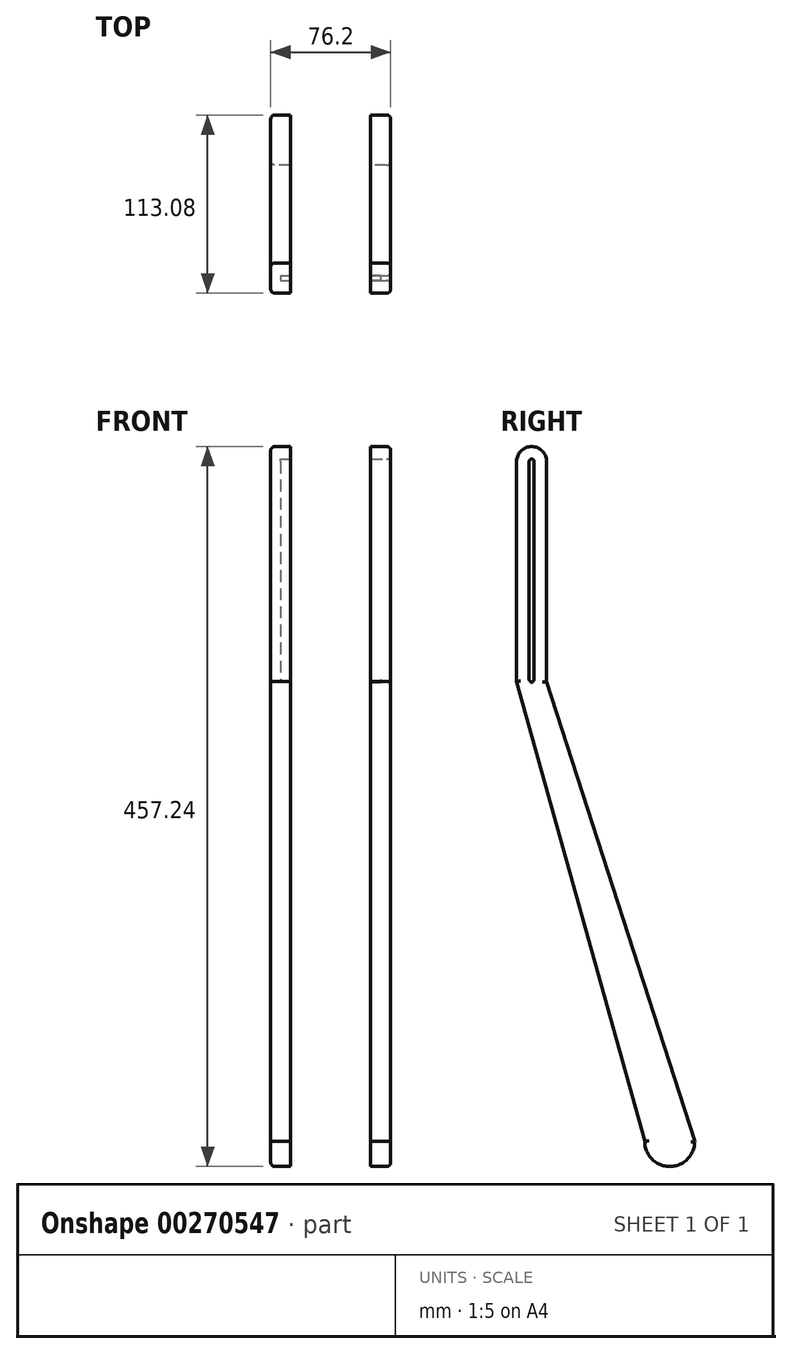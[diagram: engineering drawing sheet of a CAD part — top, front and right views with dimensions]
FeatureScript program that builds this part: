
annotation { "Feature Type Name" : "Feature", "Feature Type Description" : "" }
export const myFeature = defineFeature(function(context is Context, id is Id, definition is map)
    precondition{}
    {
        {
            var Q0;
            Q0=qCreatedBy(makeId("Right.planeOp"),FACE);
            var sketch = newSketch(context, id + "F0", { "sketchPlane" : qUnion([Q0])});
            skLineSegment(sketch, "E0", {"start": v(0, 0) * mm, "end": v(0, 355.6) * mm, "construction": true});
            skLineSegment(sketch, "E1", {"start": v(19.3, 0) * mm, "end": v(-74.73, 292.1) * mm});
            skLineSegment(sketch, "E2", {"start": v(-74.73, 292.1) * mm, "end": v(-93.78, 292.1) * mm});
            skLineSegment(sketch, "E3", {"start": v(-93.78, 292.1) * mm, "end": v(-12.45, 0) * mm});
            skLineSegment(sketch, "E4", {"start": v(-93.78, 292.1) * mm, "end": v(-93.78, 431.8) * mm});
            skLineSegment(sketch, "E5", {"start": v(-93.78, 431.8) * mm, "end": v(-74.73, 431.8) * mm});
            skLineSegment(sketch, "E6", {"start": v(-74.73, 431.8) * mm, "end": v(-74.73, 292.1) * mm});
            skArc(sketch, "E7", {"start": v(-74.73, 431.8) * mm, "mid": v(-84.26, 441.33) * mm, "end": v(-93.78, 431.8) * mm});
            skLineSegment(sketch, "E8", {"start": v(-12.45, 0) * mm, "end": v(19.3, 0) * mm});
            skArc(sketch, "E9", {"start": v(-12.45, 0) * mm, "mid": v(3.43, -15.91) * mm, "end": v(19.3, 0) * mm});
            skSolve(sketch);
        }
        {
            var Q0;
            Q0 = qSketchRegion(id + "F0", true);
            extrude(context, id + "F1", {"entities" : qUnion([Q0]), "depth" : 127 * mm});
        }
        {
            var Q0;
            Q0=makeQuery(id+"F1.opExtrude","CAP_FACE",FACE,{"disambiguationData":[OSD([sQuery(id+"F0.wireOp",EDGE,"E1"),sQuery(id+"F0.wireOp",EDGE,"E3"),sQuery(id+"F0.wireOp",EDGE,"E4"),sQuery(id+"F0.wireOp",EDGE,"E6"),sQuery(id+"F0.wireOp",EDGE,"E7"),sQuery(id+"F0.wireOp",EDGE,"vNp1OqKy-Z6YU-8cuM-Ckrt-ocsQJN6kqNDd"),sQuery(id+"F0.wireOp",EDGE,"EuecpMSg-LQ6o-H8uq-qzqB-xBjWzeGu6t28"),sQuery(id+"F0.wireOp",EDGE,"25FLd6Fp-RHUA-4MTj-8GUR-LZmMyovwXqkN"),sQuery(id+"F0.wireOp",EDGE,"Zij4NibO-UUHo-Tc3n-FIWC-QqlzmEsbWXEq")])],"isStart":false});
            var sketch = newSketch(context, id + "F2", { "sketchPlane" : qUnion([Q0])});
            skLineSegment(sketch, "E10", {"start": v(36.72, -144.12) * mm, "end": v(-159.05, 242.08) * mm});
            skLineSegment(sketch, "E11", {"start": v(-159.05, 242.08) * mm, "end": v(-331.56, 331.76) * mm});
            skLineSegment(sketch, "E12", {"start": v(-331.56, 331.76) * mm, "end": v(-175.34, 764.32) * mm});
            skLineSegment(sketch, "E13", {"start": v(-175.34, 764.32) * mm, "end": v(-62.3, 748.79) * mm});
            skLineSegment(sketch, "E14", {"start": v(-62.3, 748.79) * mm, "end": v(32.9, 331.76) * mm});
            skLineSegment(sketch, "E15", {"start": v(32.9, 331.76) * mm, "end": v(36.72, -144.12) * mm});
            skSolve(sketch);
        }
        {
            var Q0;
            Q0 = qSketchRegion(id + "F2", true);
            extrude(context, id + "F3", {"entities" : qUnion([Q0]), "operationType" : NewBodyOperationType.REMOVE, "oppositeDirection" : true, "depth" : 25.4 * mm});
        }
        {
            var Q0;
            Q0=makeQuery(id+"F1.opExtrude","CAP_FACE",FACE,{"disambiguationData":[OSD([sQuery(id+"F0.wireOp",EDGE,"E1"),sQuery(id+"F0.wireOp",EDGE,"E3"),sQuery(id+"F0.wireOp",EDGE,"E4"),sQuery(id+"F0.wireOp",EDGE,"E6"),sQuery(id+"F0.wireOp",EDGE,"E7"),sQuery(id+"F0.wireOp",EDGE,"vNp1OqKy-Z6YU-8cuM-Ckrt-ocsQJN6kqNDd"),sQuery(id+"F0.wireOp",EDGE,"EuecpMSg-LQ6o-H8uq-qzqB-xBjWzeGu6t28"),sQuery(id+"F0.wireOp",EDGE,"25FLd6Fp-RHUA-4MTj-8GUR-LZmMyovwXqkN"),sQuery(id+"F0.wireOp",EDGE,"Zij4NibO-UUHo-Tc3n-FIWC-QqlzmEsbWXEq")])],"isStart":true});
            var sketch = newSketch(context, id + "F4", { "sketchPlane" : qUnion([Q0])});
            skLineSegment(sketch, "E16", {"start": v(19.52, -53.18) * mm, "end": v(215.46, 252.99) * mm});
            skLineSegment(sketch, "E17", {"start": v(215.46, 252.99) * mm, "end": v(223.34, 387.87) * mm});
            skLineSegment(sketch, "E18", {"start": v(223.34, 387.87) * mm, "end": v(148.2, 484.06) * mm});
            skLineSegment(sketch, "E19", {"start": v(148.2, 484.06) * mm, "end": v(63.85, 484.06) * mm});
            skLineSegment(sketch, "E20", {"start": v(63.85, 484.06) * mm, "end": v(-113.5, 45.4) * mm});
            skLineSegment(sketch, "E21", {"start": v(-113.5, 45.4) * mm, "end": v(19.52, -53.18) * mm});
            skSolve(sketch);
        }
        {
            var Q0;
            Q0 = qSketchRegion(id + "F4", true);
            extrude(context, id + "F5", {"entities" : qUnion([Q0]), "operationType" : NewBodyOperationType.REMOVE, "oppositeDirection" : true, "depth" : 25.4 * mm});
        }
        {
            var Q0;
            Q0=makeQuery(id+"F1.opExtrude","SWEPT_FACE",FACE,{"disambiguationData":[OSD([sQuery(id+"F0.wireOp",EDGE,"E4")])]});
            var sketch = newSketch(context, id + "F6", { "sketchPlane" : qUnion([Q0])});
            skLineSegment(sketch, "E22.left", {"start": v(88.9, -69.31) * mm, "end": v(88.9, 482.6) * mm});
            skLineSegment(sketch, "E22.right", {"start": v(38.1, -69.31) * mm, "end": v(38.1, 482.6) * mm});
            skLineSegment(sketch, "E23", {"start": v(38.1, 482.6) * mm, "end": v(88.9, 482.6) * mm});
            skLineSegment(sketch, "E24", {"start": v(38.1, -69.31) * mm, "end": v(88.9, -69.31) * mm});
            skSolve(sketch);
        }
        {
            var Q0;
            Q0 = qSketchRegion(id + "F6", true);
            extrude(context, id + "F7", {"entities" : qUnion([Q0]), "operationType" : NewBodyOperationType.REMOVE, "endBound" : BoundingType.THROUGH_ALL, "oppositeDirection" : true, "depth" : 25.4 * mm});
        }
        {
            var Q0;
            Q0=makeQuery(id+"F7.boolean.opBoolean","COPY",FACE,{"derivedFrom":makeQuery(id+"F7.opExtrude","SWEPT_FACE",FACE,{"disambiguationData":[OSD([sQuery(id+"F6.wireOp",EDGE,"E22.right")])]})});
            var sketch = newSketch(context, id + "F8", { "sketchPlane" : qUnion([Q0])});
            skLineSegment(sketch, "E25", {"start": v(-84.26, 431.8) * mm, "end": v(-84.26, 293.52) * mm, "construction": true});
            skLineSegment(sketch, "E26.bottom", {"start": v(-85.84, 431.8) * mm, "end": v(-82.67, 431.8) * mm});
            skLineSegment(sketch, "E26.top", {"start": v(-85.84, 293.52) * mm, "end": v(-82.67, 293.52) * mm});
            skLineSegment(sketch, "E26.left", {"start": v(-85.84, 431.8) * mm, "end": v(-85.84, 293.52) * mm});
            skLineSegment(sketch, "E26.right", {"start": v(-82.67, 431.8) * mm, "end": v(-82.67, 293.52) * mm});
            skPoint(sketch, "E26.middle", {"position": v(-84.26, 362.66) * mm});
            skArc(sketch, "E27", {"start": v(-82.67, 431.8) * mm, "mid": v(-84.26, 433.39) * mm, "end": v(-85.84, 431.8) * mm});
            skArc(sketch, "E28", {"start": v(-85.84, 293.52) * mm, "mid": v(-84.26, 291.93) * mm, "end": v(-82.67, 293.52) * mm});
            skSolve(sketch);
        }
        {
            var Q0;
            Q0 = qSketchRegion(id + "F8", true);
            extrude(context, id + "F9", {"entities" : qUnion([Q0]), "operationType" : NewBodyOperationType.REMOVE, "oppositeDirection" : true, "depth" : 6.35 * mm, "hasSecondDirection" : true, "secondDirectionOppositeDirection" : false, "secondDirectionDepth" : 177.55 * mm});
        }
        {
            var Q0;
            Q0=makeQuery(id+"F7.boolean.opBoolean","COPY",FACE,{"derivedFrom":makeQuery(id+"F7.opExtrude","SWEPT_FACE",FACE,{"disambiguationData":[OSD([sQuery(id+"F6.wireOp",EDGE,"E22.left")])]})});
            var sketch = newSketch(context, id + "F10", { "sketchPlane" : qUnion([Q0])});
            skLineSegment(sketch, "E29", {"start": v(84.26, 431.1) * mm, "end": v(84.26, 292.8) * mm, "construction": true});
            skLineSegment(sketch, "E30.bottom", {"start": v(82.67, 431.1) * mm, "end": v(85.84, 431.1) * mm});
            skLineSegment(sketch, "E30.top", {"start": v(82.67, 292.8) * mm, "end": v(85.84, 292.8) * mm});
            skLineSegment(sketch, "E30.left", {"start": v(82.67, 431.1) * mm, "end": v(82.67, 292.8) * mm});
            skLineSegment(sketch, "E30.right", {"start": v(85.84, 431.1) * mm, "end": v(85.84, 292.8) * mm});
            skPoint(sketch, "E30.middle", {"position": v(84.26, 361.95) * mm});
            skArc(sketch, "E31", {"start": v(85.84, 431.1) * mm, "mid": v(84.26, 432.68) * mm, "end": v(82.67, 431.1) * mm});
            skArc(sketch, "E32", {"start": v(82.67, 292.8) * mm, "mid": v(84.26, 291.22) * mm, "end": v(85.84, 292.8) * mm});
            skPoint(sketch, "E33", {"position": v(84.26, 441.33) * mm});
            skPoint(sketch, "E34", {"position": v(93.78, 361.95) * mm});
            skSolve(sketch);
        }
        {
            var Q0;
            Q0 = qSketchRegion(id + "F10", true);
            extrude(context, id + "F11", {"entities" : qUnion([Q0]), "operationType" : NewBodyOperationType.REMOVE, "oppositeDirection" : true, "depth" : 6.35 * mm});
        }
        {
            var Q0;
            Q0=makeQuery(id+"F5.boolean.opBoolean","COPY",FACE,{"derivedFrom":makeQuery(id+"F5.opExtrude","CAP_FACE",FACE,{"disambiguationData":[OSD([sQuery(id+"F4.wireOp",EDGE,"E16"),sQuery(id+"F4.wireOp",EDGE,"E17"),sQuery(id+"F4.wireOp",EDGE,"E18"),sQuery(id+"F4.wireOp",EDGE,"E19"),sQuery(id+"F4.wireOp",EDGE,"E20"),sQuery(id+"F4.wireOp",EDGE,"E21")])],"isStart":false})});
            fillet(context, id + "F12", {"entities" : qUnion([Q0]), "radius" : 2.54 * mm, "tangentPropagation" : true, "allowEdgeOverflow" : false});
        }
        {
            var Q0;
            Q0=makeQuery(id+"F3.boolean.opBoolean","COPY",FACE,{"derivedFrom":makeQuery(id+"F3.opExtrude","CAP_FACE",FACE,{"disambiguationData":[OSD([sQuery(id+"F2.wireOp",EDGE,"E10"),sQuery(id+"F2.wireOp",EDGE,"E11"),sQuery(id+"F2.wireOp",EDGE,"E12"),sQuery(id+"F2.wireOp",EDGE,"E13"),sQuery(id+"F2.wireOp",EDGE,"E14"),sQuery(id+"F2.wireOp",EDGE,"E15")])],"isStart":false})});
            fillet(context, id + "F13", {"entities" : qUnion([Q0]), "radius" : 2.54 * mm, "tangentPropagation" : true, "allowEdgeOverflow" : false});
        }
    });
